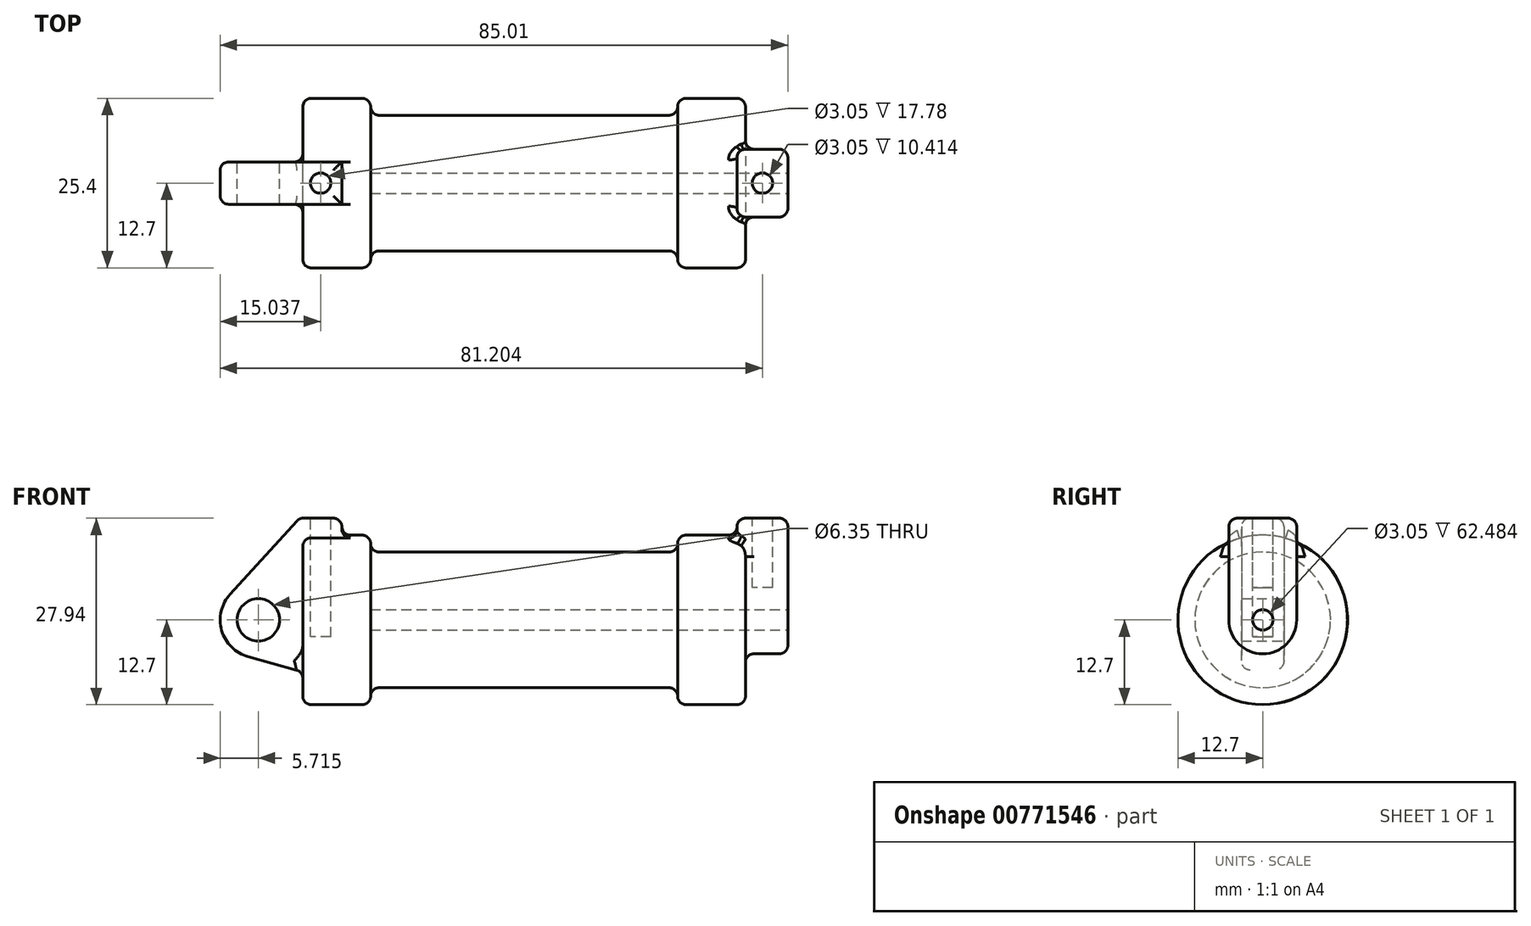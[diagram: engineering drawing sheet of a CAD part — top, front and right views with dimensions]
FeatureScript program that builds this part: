
annotation { "Feature Type Name" : "Feature", "Feature Type Description" : "" }
export const myFeature = defineFeature(function(context is Context, id is Id, definition is map)
    precondition{}
    {
        {
            var Q0;
            Q0=qCreatedBy(makeId("Front.planeOp"),FACE);
            var sketch = newSketch(context, id + "F0", { "sketchPlane" : qUnion([Q0])});
            skLineSegment(sketch, "E0", {"start": v(0, 0) * mm, "end": v(0, 12.7) * mm});
            skLineSegment(sketch, "E1", {"start": v(0, 12.7) * mm, "end": v(10.16, 12.7) * mm});
            skLineSegment(sketch, "E2", {"start": v(10.16, 12.7) * mm, "end": v(10.16, 10.16) * mm});
            skLineSegment(sketch, "E3", {"start": v(10.16, 10.16) * mm, "end": v(56.13, 10.16) * mm});
            skLineSegment(sketch, "E4", {"start": v(56.13, 10.16) * mm, "end": v(56.13, 12.7) * mm});
            skLineSegment(sketch, "E5", {"start": v(56.13, 12.7) * mm, "end": v(66.3, 12.7) * mm});
            skLineSegment(sketch, "E6", {"start": v(66.3, 12.7) * mm, "end": v(66.3, 0) * mm});
            skLineSegment(sketch, "E7", {"start": v(66.3, 0) * mm, "end": v(0, 0) * mm});
            skLineSegment(sketch, "E8", {"start": v(5.84, 15.24) * mm, "end": v(-0.5, 15.24) * mm});
            skLineSegment(sketch, "E9", {"start": v(-0.5, 15.24) * mm, "end": v(-10.88, 3.85) * mm});
            skLineSegment(sketch, "E10", {"start": v(0, 0) * mm, "end": v(-6.65, 0) * mm});
            skCircle(sketch, "E11", {"center": v(-6.65, 0) * mm, "radius": 5.72 * mm});
            skCircle(sketch, "E12", {"center": v(-6.65, 0) * mm, "radius": 3.18 * mm});
            skLineSegment(sketch, "E13", {"start": v(5.84, 15.24) * mm, "end": v(5.84, -9.4) * mm});
            skLineSegment(sketch, "E14", {"start": v(5.84, -9.4) * mm, "end": v(-8.18, -5.5) * mm});
            skSolve(sketch);
        }
        {
            var Q0;
            {var subQ0=sQuery(id+"F0.wireOp",EDGE,"E2");Q0=makeQuery(id+"F0.imprint","IMPRINT",FACE,{"disambiguationData":[TD([[makeQuery(id+"F0.imprint","IMPRINT",EDGE,{"derivedFrom":subQ0}),-1.0]])]});}
            var Q1;
            {var subQ0=sQuery(id+"F0.wireOp",EDGE,"E0");Q1=makeQuery(id+"F0.imprint","IMPRINT",FACE,{"disambiguationData":[TD([[makeQuery(id+"F0.imprint","IMPRINT",EDGE,{"derivedFrom":subQ0}),-1.0]])]});}
            var Q2;
            Q2=sQuery(id+"F0.wireOp",EDGE,"E7");
            revolve(context, id + "F1", {"surfaceOperationType" : NewSurfaceOperationType.NEW, "entities" : qUnion([Q0, Q1]), "axis" : qUnion([Q2]), "revolveType" : RevolveType.FULL});
        }
        {
            var Q0;
            {var subQ0=sQuery(id+"F0.wireOp",EDGE,"E14");Q0=makeQuery(id+"F0.imprint","IMPRINT",FACE,{"disambiguationData":[TD([[makeQuery(id+"F0.imprint","IMPRINT",EDGE,{"derivedFrom":subQ0}),-1.0]])]});}
            var Q1;
            {var subQ1=sQuery(id+"F0.wireOp",EDGE,"E0");Q1=makeQuery(id+"F0.imprint","IMPRINT",FACE,{"disambiguationData":[TD([[makeQuery(id+"F0.imprint","IMPRINT",EDGE,{"derivedFrom":subQ1}),1.0]])]});}
            var Q2;
            {var subQ0=sQuery(id+"F0.wireOp",EDGE,"E0");Q2=makeQuery(id+"F0.imprint","IMPRINT",FACE,{"disambiguationData":[TD([[makeQuery(id+"F0.imprint","IMPRINT",EDGE,{"derivedFrom":subQ0}),-1.0]])]});}
            var Q3;
            {var subQ5=sQuery(id+"F0.wireOp",EDGE,"E12");Q3=makeQuery(id+"F0.imprint","IMPRINT",FACE,{"disambiguationData":[TD([[makeQuery(id+"F0.imprint","IMPRINT",EDGE,{"derivedFrom":subQ5}),-1.0]])]});}
            extrude(context, id + "F2", {"entities" : qUnion([Q0, Q1, Q2, Q3]), "operationType" : NewBodyOperationType.ADD, "endBound" : BoundingType.SYMMETRIC, "depth" : 6.35 * mm, "offsetDistance" : 25.4 * mm});
        }
        {
            var Q0;
            Q0=makeQuery(id+"F1.opRevolve","SWEPT_FACE",FACE,{"disambiguationData":[OSD([sQuery(id+"F0.wireOp",EDGE,"E6")])]});
            var sketch = newSketch(context, id + "F3", { "sketchPlane" : qUnion([Q0])});
            skCircle(sketch, "E15", {"center": v(0, 0) * mm, "radius": 1.52 * mm});
            skCircle(sketch, "E16", {"center": v(0, 0) * mm, "radius": 5.08 * mm});
            skLineSegment(sketch, "E17", {"start": v(-5.08, 0) * mm, "end": v(-5.08, 15.24) * mm});
            skLineSegment(sketch, "E18", {"start": v(-5.08, 15.24) * mm, "end": v(5.08, 15.24) * mm});
            skLineSegment(sketch, "E19", {"start": v(5.08, 15.24) * mm, "end": v(5.08, 0) * mm});
            skSolve(sketch);
        }
        {
            var Q0;
            Q0=makeQuery(id+"F3.imprint","IMPRINT",FACE,{"disambiguationData":[TD([[makeQuery(id+"F3.imprint","IMPRINT",EDGE,{"derivedFrom":sQuery(id+"F3.wireOp",EDGE,"E15")}),-1.0]])]});
            var Q1;
            {var subQ0=sQuery(id+"F3.wireOp",EDGE,"E17");var subQ1=sQuery(id+"F3.wireOp",EDGE,"E16");var subQ2=makeQuery(id+"F3.imprint","INTERSECT",VERTEX,{"derivedFrom":[subQ1,subQ0]});Q1=makeQuery(id+"F3.imprint","IMPRINT",FACE,{"disambiguationData":[TD([[makeQuery(id+"F3.imprint","IMPRINT",EDGE,{"disambiguationData":[TD([[subQ2,1.0]])],"derivedFrom":subQ1}),-1.0]])]});}
            var Q2;
            {var subQ0=sQuery(id+"F3.wireOp",EDGE,"E18");Q2=makeQuery(id+"F3.imprint","IMPRINT",FACE,{"disambiguationData":[TD([[makeQuery(id+"F3.imprint","IMPRINT",EDGE,{"derivedFrom":subQ0}),-1.0]])]});}
            var Q3;
            Q3=makeQuery(id+"F3.imprint","IMPRINT",FACE,{"disambiguationData":[TD([[makeQuery(id+"F3.imprint","IMPRINT",EDGE,{"derivedFrom":sQuery(id+"F3.wireOp",EDGE,"E15")}),1.0]])]});
            extrude(context, id + "F4", {"entities" : qUnion([Q0, Q1, Q2, Q3]), "operationType" : NewBodyOperationType.ADD, "depth" : 6.35 * mm, "offsetDistance" : 25.4 * mm, "hasSecondDirection" : true, "secondDirectionOppositeDirection" : true, "secondDirectionDepth" : 1.27 * mm});
        }
        {
            var Q0;
            Q0=makeQuery(id+"F3.imprint","IMPRINT",FACE,{"disambiguationData":[TD([[makeQuery(id+"F3.imprint","IMPRINT",EDGE,{"derivedFrom":sQuery(id+"F3.wireOp",EDGE,"E15")}),1.0]])]});
            var Q1;
            Q1=makeQuery(id+"F1.opRevolve","SWEPT_FACE",FACE,{"disambiguationData":[OSD([sQuery(id+"F0.wireOp",EDGE,"E2")])]});
            var Q2;
            Q2=makeQuery(id+"F4.opExtrude","CAP_FACE",FACE,{"disambiguationData":[OSD([sQuery(id+"F3.wireOp",EDGE,"E16"),sQuery(id+"F3.wireOp",EDGE,"E17"),sQuery(id+"F3.wireOp",EDGE,"E18"),sQuery(id+"F3.wireOp",EDGE,"E19")])],"isStart":false});
            extrude(context, id + "F5", {"entities" : qUnion([Q0]), "operationType" : NewBodyOperationType.REMOVE, "endBound" : BoundingType.UP_TO_SURFACE, "oppositeDirection" : true, "depth" : 25.4 * mm, "endBoundEntityFace" : qUnion([Q1]), "offsetDistance" : 25.4 * mm, "hasSecondDirection" : true, "secondDirectionBound" : SecondDirectionBoundingType.UP_TO_SURFACE, "secondDirectionOppositeDirection" : false, "secondDirectionDepth" : 25.4 * mm, "secondDirectionBoundEntityFace" : qUnion([Q2])});
        }
        {
            var Q0;
            Q0=makeQuery(id+"F4.opExtrude","SWEPT_FACE",FACE,{"disambiguationData":[OSD([sQuery(id+"F3.wireOp",EDGE,"E18")])]});
            var sketch = newSketch(context, id + "F6", { "sketchPlane" : qUnion([Q0])});
            skCircle(sketch, "E20", {"center": v(68.83, 0) * mm, "radius": 1.52 * mm});
            skPoint(sketch, "E20.centerSnap0", {"position": v(72.64, 0) * mm});
            skPoint(sketch, "E20.centerSnap1", {"position": v(68.83, 5.08) * mm});
            skSolve(sketch);
        }
        {
            var Q0;
            Q0=makeQuery(id+"F2.opExtrude","SWEPT_FACE",FACE,{"disambiguationData":[OSD([sQuery(id+"F0.wireOp",EDGE,"E8")])]});
            var sketch = newSketch(context, id + "F7", { "sketchPlane" : qUnion([Q0])});
            skCircle(sketch, "E21", {"center": v(2.67, 0) * mm, "radius": 1.52 * mm});
            skPoint(sketch, "E21.centerSnap0", {"position": v(5.84, 0) * mm});
            skPoint(sketch, "E21.centerSnap1", {"position": v(2.67, 3.18) * mm});
            skSolve(sketch);
        }
        {
            var Q0;
            Q0=makeQuery(id+"F7.imprint","IMPRINT",FACE,{"disambiguationData":[TD([[makeQuery(id+"F7.imprint","IMPRINT",EDGE,{"derivedFrom":sQuery(id+"F7.wireOp",EDGE,"E21")}),1.0]])]});
            extrude(context, id + "F8", {"entities" : qUnion([Q0]), "operationType" : NewBodyOperationType.REMOVE, "oppositeDirection" : true, "depth" : 17.78 * mm, "offsetDistance" : 25.4 * mm});
        }
        {
            var Q0;
            Q0=makeQuery(id+"F6.imprint","IMPRINT",FACE,{"disambiguationData":[TD([[makeQuery(id+"F6.imprint","IMPRINT",EDGE,{"derivedFrom":sQuery(id+"F6.wireOp",EDGE,"E20")}),1.0]])]});
            extrude(context, id + "F9", {"entities" : qUnion([Q0]), "operationType" : NewBodyOperationType.REMOVE, "oppositeDirection" : true, "depth" : 10.4 * mm, "offsetDistance" : 25.4 * mm});
        }
        {
            var Q0;
            Q0=makeQuery(id+"F1.opRevolve","SWEPT_EDGE",EDGE,{"disambiguationData":[OSD([sQuery(id+"F0.wireOp",EDGE,"E5"),sQuery(id+"F0.wireOp",EDGE,"E6")])]});
            var Q1;
            Q1=makeQuery(id+"F1.opRevolve","SWEPT_EDGE",EDGE,{"disambiguationData":[OSD([sQuery(id+"F0.wireOp",EDGE,"E4"),sQuery(id+"F0.wireOp",EDGE,"E5")])]});
            var Q2;
            Q2=makeQuery(id+"F1.opRevolve","SWEPT_EDGE",EDGE,{"disambiguationData":[OSD([sQuery(id+"F0.wireOp",EDGE,"E3"),sQuery(id+"F0.wireOp",EDGE,"E4")])]});
            var Q3;
            Q3=makeQuery(id+"F1.opRevolve","SWEPT_EDGE",EDGE,{"disambiguationData":[OSD([sQuery(id+"F0.wireOp",EDGE,"E1"),sQuery(id+"F0.wireOp",EDGE,"E2")])]});
            var Q4;
            Q4=makeQuery(id+"F1.opRevolve","SWEPT_EDGE",EDGE,{"disambiguationData":[OSD([sQuery(id+"F0.wireOp",EDGE,"E0"),sQuery(id+"F0.wireOp",EDGE,"E1")])]});
            var Q5;
            Q5=makeQuery(id+"F1.opRevolve","SWEPT_EDGE",EDGE,{"disambiguationData":[OSD([sQuery(id+"F0.wireOp",EDGE,"E2"),sQuery(id+"F0.wireOp",EDGE,"E3")])]});
            fillet(context, id + "F10", {"entities" : qUnion([Q0, Q1, Q2, Q3, Q4, Q5]), "radius" : 1.27 * mm, "tangentPropagation" : true, "allowEdgeOverflow" : false});
        }
        {
            var Q0;
            Q0=makeQuery(id+"F2.opExtrude","CAP_EDGE",EDGE,{"disambiguationData":[OSD([sQuery(id+"F0.wireOp",EDGE,"E9")])],"isStart":false});
            var Q1;
            Q1=makeQuery(id+"F2.opExtrude","CAP_EDGE",EDGE,{"disambiguationData":[OSD([sQuery(id+"F0.wireOp",EDGE,"E8")])],"isStart":false});
            var Q2;
            Q2=makeQuery(id+"F2.opExtrude","SWEPT_EDGE",EDGE,{"disambiguationData":[OSD([sQuery(id+"F0.wireOp",EDGE,"E8"),sQuery(id+"F0.wireOp",EDGE,"E9")])]});
            var Q3;
            Q3=makeQuery(id+"F2.opExtrude","SWEPT_EDGE",EDGE,{"disambiguationData":[OSD([sQuery(id+"F0.wireOp",EDGE,"E8"),sQuery(id+"F0.wireOp",EDGE,"E13")])]});
            var Q4;
            Q4=makeQuery(id+"F2.opExtrude","CAP_EDGE",EDGE,{"disambiguationData":[OSD([sQuery(id+"F0.wireOp",EDGE,"E8")])],"isStart":true});
            var Q5;
            Q5=makeQuery(id+"F2.opExtrude","CAP_EDGE",EDGE,{"disambiguationData":[OSD([sQuery(id+"F0.wireOp",EDGE,"E9")])],"isStart":true});
            var Q6;
            Q6=makeQuery(id+"F2.boolean.opBoolean","INTERSECT",EDGE,{"derivedFrom":[makeQuery(id+"F1.opRevolve","SWEPT_FACE",FACE,{"disambiguationData":[OSD([sQuery(id+"F0.wireOp",EDGE,"E0")])]}),makeQuery(id+"F2.opExtrude","SWEPT_FACE",FACE,{"disambiguationData":[OSD([sQuery(id+"F0.wireOp",EDGE,"E14")])]})]});
            var Q7;
            Q7=makeQuery(id+"F2.boolean.opBoolean","INTERSECT",EDGE,{"derivedFrom":[makeQuery(id+"F1.opRevolve","SWEPT_FACE",FACE,{"disambiguationData":[OSD([sQuery(id+"F0.wireOp",EDGE,"E1")])]}),makeQuery(id+"F2.opExtrude","SWEPT_FACE",FACE,{"disambiguationData":[OSD([sQuery(id+"F0.wireOp",EDGE,"E13")])]})]});
            fillet(context, id + "F11", {"entities" : qUnion([Q0, Q1, Q2, Q3, Q4, Q5, Q6, Q7]), "radius" : 1.27 * mm, "tangentPropagation" : true, "allowEdgeOverflow" : false});
        }
        {
            var Q0;
            Q0=makeQuery(id+"F4.opExtrude","CAP_EDGE",EDGE,{"disambiguationData":[OSD([sQuery(id+"F3.wireOp",EDGE,"E17")])],"isStart":false});
            var Q1;
            Q1=makeQuery(id+"F4.opExtrude","CAP_EDGE",EDGE,{"disambiguationData":[OSD([sQuery(id+"F3.wireOp",EDGE,"E18")])],"isStart":true});
            var Q2;
            Q2=makeQuery(id+"F4.opExtrude","SWEPT_EDGE",EDGE,{"disambiguationData":[OSD([sQuery(id+"F3.wireOp",EDGE,"E17"),sQuery(id+"F3.wireOp",EDGE,"E18")])]});
            var Q3;
            Q3=makeQuery(id+"F4.opExtrude","CAP_EDGE",EDGE,{"disambiguationData":[OSD([sQuery(id+"F3.wireOp",EDGE,"E18")])],"isStart":false});
            var Q4;
            Q4=makeQuery(id+"F4.opExtrude","SWEPT_EDGE",EDGE,{"disambiguationData":[OSD([sQuery(id+"F3.wireOp",EDGE,"E18"),sQuery(id+"F3.wireOp",EDGE,"E19")])]});
            var Q5;
            Q5=makeQuery(id+"F4.boolean.opBoolean","INTERSECT",EDGE,{"derivedFrom":[makeQuery(id+"F1.opRevolve","SWEPT_FACE",FACE,{"disambiguationData":[OSD([sQuery(id+"F0.wireOp",EDGE,"E6")])]}),makeQuery(id+"F4.opExtrude","SWEPT_FACE",FACE,{"disambiguationData":[OSD([sQuery(id+"F3.wireOp",EDGE,"E19")])]})]});
            var Q6;
            Q6=makeQuery(id+"F4.boolean.opBoolean","INTERSECT",EDGE,{"derivedFrom":[makeQuery(id+"F1.opRevolve","SWEPT_FACE",FACE,{"disambiguationData":[OSD([sQuery(id+"F0.wireOp",EDGE,"E6")])]}),makeQuery(id+"F4.opExtrude","SWEPT_FACE",FACE,{"disambiguationData":[OSD([sQuery(id+"F3.wireOp",EDGE,"E16")])]})]});
            var Q7;
            Q7=makeQuery(id+"F4.boolean.opBoolean","INTERSECT",EDGE,{"derivedFrom":[makeQuery(id+"F1.opRevolve","SWEPT_FACE",FACE,{"disambiguationData":[OSD([sQuery(id+"F0.wireOp",EDGE,"E6")])]}),makeQuery(id+"F4.opExtrude","SWEPT_FACE",FACE,{"disambiguationData":[OSD([sQuery(id+"F3.wireOp",EDGE,"E17")])]})]});
            var Q8;
            Q8=makeQuery(id+"F4.opExtrude","CAP_EDGE",EDGE,{"disambiguationData":[OSD([sQuery(id+"F3.wireOp",EDGE,"E16")])],"isStart":false});
            var Q9;
            Q9=makeQuery(id+"F4.opExtrude","CAP_EDGE",EDGE,{"disambiguationData":[OSD([sQuery(id+"F3.wireOp",EDGE,"E19")])],"isStart":false});
            var Q10;
            Q10=makeQuery(id+"F4.boolean.opBoolean","INTERSECT",EDGE,{"derivedFrom":[makeQuery(id+"F1.opRevolve","SWEPT_FACE",FACE,{"disambiguationData":[OSD([sQuery(id+"F0.wireOp",EDGE,"E5")])]}),makeQuery(id+"F4.opExtrude","CAP_FACE",FACE,{"disambiguationData":[OSD([sQuery(id+"F3.wireOp",EDGE,"E16"),sQuery(id+"F3.wireOp",EDGE,"E17"),sQuery(id+"F3.wireOp",EDGE,"E18"),sQuery(id+"F3.wireOp",EDGE,"E19")])],"isStart":true})]});
            var Q11;
            Q11=makeQuery(id+"F4.opExtrude","CAP_EDGE",EDGE,{"disambiguationData":[OSD([sQuery(id+"F3.wireOp",EDGE,"E17")])],"isStart":true});
            var Q12;
            Q12=makeQuery(id+"F4.opExtrude","CAP_EDGE",EDGE,{"disambiguationData":[OSD([sQuery(id+"F3.wireOp",EDGE,"E19")])],"isStart":true});
            fillet(context, id + "F12", {"entities" : qUnion([Q0, Q1, Q2, Q3, Q4, Q5, Q6, Q7, Q8, Q9, Q10, Q11, Q12]), "radius" : 1.27 * mm, "tangentPropagation" : true, "allowEdgeOverflow" : false});
        }
    });
